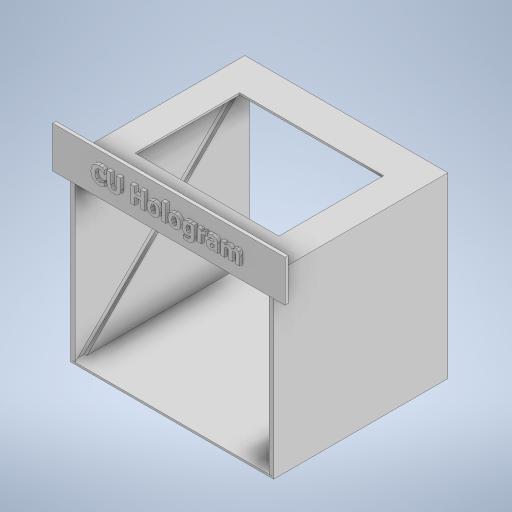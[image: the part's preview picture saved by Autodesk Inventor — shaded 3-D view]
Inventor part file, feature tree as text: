
AUTODESK INVENTOR PART (.ipt)
format: ipt  version: 2024 (Build 280153000, 153)  size: 564,736 bytes
history: native  units: mm
features: extrude x11, sketch x11
ambient origin geometry x8: Origin, YZ Plane, XZ Plane, XY Plane, X Axis, Y Axis, Z Axis, Center Point
bodies: Solid1 (feature_tree)
feature tree (22):
  extrude  "Top"  Depth=160.0mm
  extrude  "Right"  Depth=179.5mm
  extrude  "Left"  Depth=304.8mm
  extrude  "Plexiglass Cut"  Depth=25.4mm
  extrude  "Bottom"  Depth=266.7mm TaperAngle=0.0deg
  extrude  "Decoration Plate"  Depth=266.7mm TaperAngle=0.0deg
  extrude  "Decoration Text"  Depth=304.8mm TaperAngle=0.0deg
  extrude  "Top Flattening"  Depth=12.7mm
  extrude  "Outer Side Flattening"  Depth=5.0mm TaperAngle=0.0deg
  extrude  "Bottom Flattening"  TaperAngle=0.0deg  [1 undecoded]
  extrude  "Inner Flattening"  TaperAngle=0.0deg  [1 undecoded]
  sketch  "Sketch1"  dims[d11=220.0mm d12=160.0mm]
  sketch  "Sketch3"  dims[d15=248.6mm d16=179.5mm]
  sketch  "Sketch4"  dims[d18=304.8mm d19=215.9mm]
  sketch  "Sketch5"  dims[d20=25.4mm d21=0.0mm d22=25.4mm]
  sketch  "Sketch6"  dims[d25=266.7mm d26=50.8mm d27=0.0mm]
  sketch  "Sketch7"  dims[d28=266.7mm d29=50.8mm d30=0.0mm]
  sketch  "Sketch8"  dims[d31=12.7mm d32=304.8mm d33=0.0mm]
  sketch  "Sketch9"  dims[d34=25.4mm d35=0.0mm d36=12.7mm]
  sketch  "Sketch10"  dims[d37=25.4mm d38=5.0mm d39=0.0mm]
  sketch  "Sketch11"  dims[d40=0.0mm d41=0.0mm]
  sketch  "Sketch12"  dims[d42=0.0mm d43=0.0mm d44=5.0mm d45=0.0mm d46=22.4mm d47=0.0mm d48=22.389425mm d49=22.389425mm d50=0.0mm d51=0.0mm d52=22.4mm d53=0.0mm d54=296.8mm d55=22.4mm d56=0.0mm]
note: 2 required parameter values undecoded (feature->parameter linkage not recoverable at this tier; creation-order binding heuristic only, values carry confidence <= 0.55)
